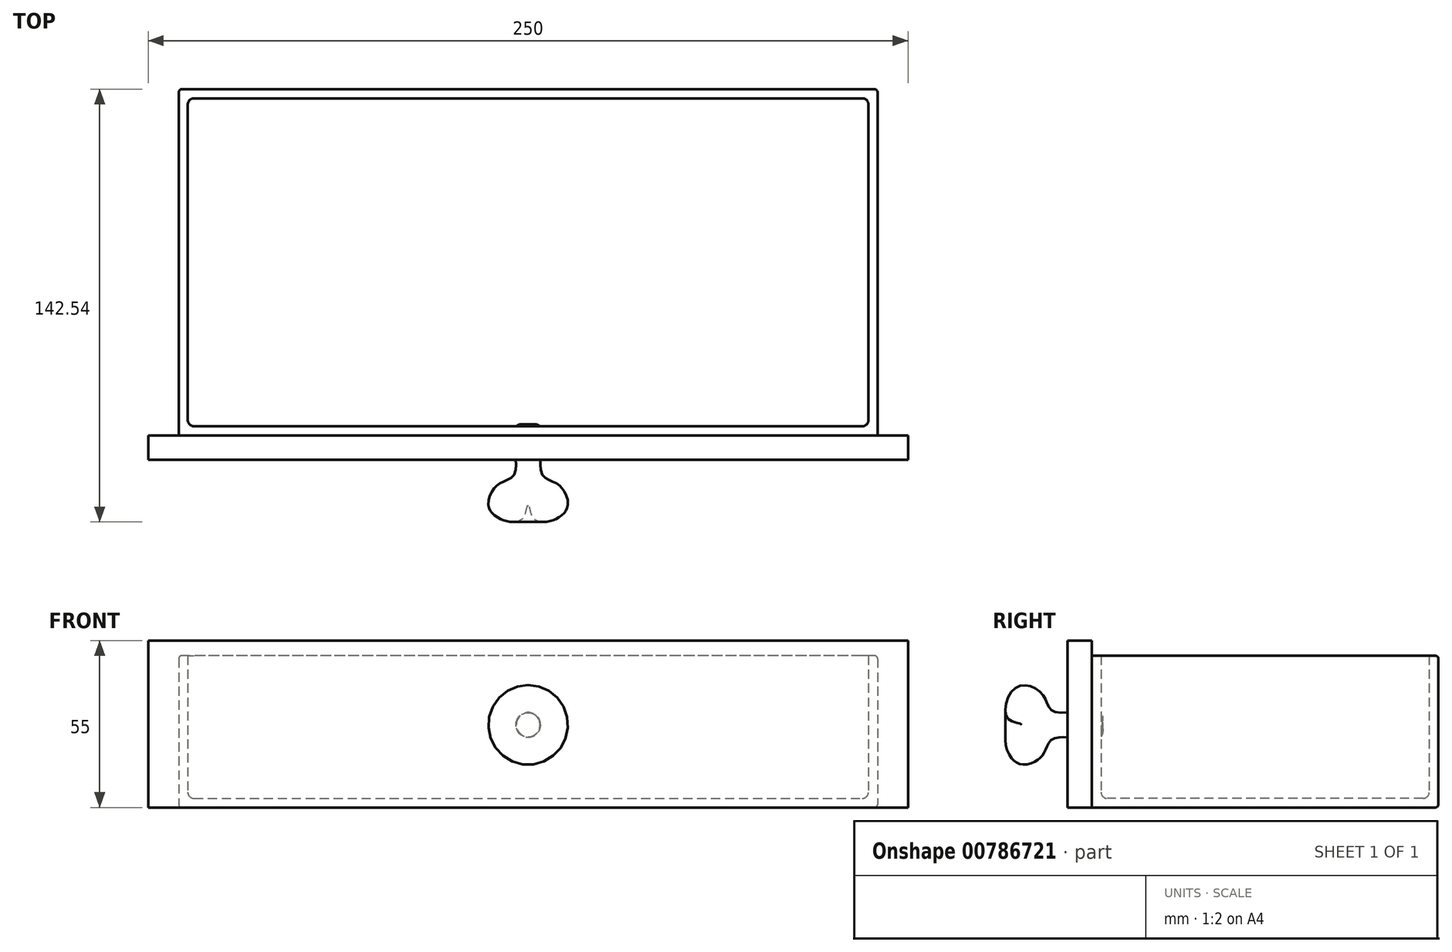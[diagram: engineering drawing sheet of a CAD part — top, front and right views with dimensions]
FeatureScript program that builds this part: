
annotation { "Feature Type Name" : "Feature", "Feature Type Description" : "" }
export const myFeature = defineFeature(function(context is Context, id is Id, definition is map)
    precondition{}
    {
        {
            var Q0;
            Q0=qCreatedBy(makeId("Top.planeOp"),FACE);
            var sketch = newSketch(context, id + "F0", { "sketchPlane" : qUnion([Q0])});
            skLineSegment(sketch, "E0.bottom", {"start": v(115, 60) * mm, "end": v(-115, 60) * mm});
            skLineSegment(sketch, "E0.right", {"start": v(-125, -54) * mm, "end": v(-125, -60) * mm});
            skPoint(sketch, "E0.middle", {"position": v(0, 0) * mm});
            skLineSegment(sketch, "E1", {"start": v(-115, 60) * mm, "end": v(-115, -54) * mm});
            skLineSegment(sketch, "E2", {"start": v(115, 60) * mm, "end": v(115, -54) * mm});
            skLineSegment(sketch, "E3", {"start": v(-115, -54) * mm, "end": v(115, -54) * mm});
            skPoint(sketch, "E4.orphan", {"position": v(125, 60) * mm});
            skPoint(sketch, "E5.orphan", {"position": v(-125, 60) * mm});
            skPoint(sketch, "E0.left.end.orphan", {"position": v(125, -60) * mm});
            skSolve(sketch);
        }
        {
            var Q0;
            Q0=qCreatedBy(makeId("Top.planeOp"),FACE);
            var sketch = newSketch(context, id + "F1", { "sketchPlane" : qUnion([Q0])});
            skLineSegment(sketch, "E6.bottom", {"start": v(125, -54) * mm, "end": v(-125, -54) * mm});
            skLineSegment(sketch, "E6.top", {"start": v(125, -62) * mm, "end": v(-125, -62) * mm});
            skLineSegment(sketch, "E6.left", {"start": v(125, -54) * mm, "end": v(125, -62) * mm});
            skLineSegment(sketch, "E6.right", {"start": v(-125, -54) * mm, "end": v(-125, -62) * mm});
            skPoint(sketch, "E6.middle", {"position": v(0, -58) * mm});
            skSolve(sketch);
        }
        {
            var Q0;
            Q0 = qSketchRegion(id + "F0", true);
            extrude(context, id + "F2", {"entities" : qUnion([Q0]), "depth" : 50 * mm, "offsetDistance" : 25 * mm});
        }
        {
            var Q0;
            Q0=makeQuery(id+"F2.opExtrude","CAP_FACE",FACE,{"disambiguationData":[OSD([sQuery(id+"F0.wireOp",EDGE,"E0.bottom"),sQuery(id+"F0.wireOp",EDGE,"E1"),sQuery(id+"F0.wireOp",EDGE,"E2"),sQuery(id+"F0.wireOp",EDGE,"E3")])],"isStart":false});
            shell(context, id + "F3", {"entities" : qUnion([Q0]), "thickness" : 3 * mm});
        }
        {
            var Q0;
            Q0=makeQuery(id+"F1.imprint","IMPRINT",FACE,{"disambiguationData":[TD([[makeQuery(id+"F1.imprint","IMPRINT",EDGE,{"derivedFrom":sQuery(id+"F1.wireOp",EDGE,"E6.bottom")}),1.0]])]});
            extrude(context, id + "F4", {"entities" : qUnion([Q0]), "operationType" : NewBodyOperationType.ADD, "depth" : 55 * mm, "offsetDistance" : 25 * mm});
        }
        {
            var Q0;
            Q0=makeQuery(id+"F3.opShell","OFFSET_FACE",FACE,{"disambiguationData":[OSD([sQuery(id+"F0.wireOp",EDGE,"E0.bottom"),sQuery(id+"F0.wireOp",EDGE,"E1"),sQuery(id+"F0.wireOp",EDGE,"E2"),sQuery(id+"F0.wireOp",EDGE,"E3")])]});
            fillet(context, id + "F5", {"entities" : qUnion([Q0]), "radius" : 2 * mm, "tangentPropagation" : true, "allowEdgeOverflow" : false});
        }
        {
            var Q0;
            Q0=makeQuery(id+"F3.opShell","OFFSET_EDGE",EDGE,{"disambiguationData":[OSD([sQuery(id+"F0.wireOp",EDGE,"E0.bottom"),sQuery(id+"F0.wireOp",EDGE,"E1")])]});
            var Q1;
            Q1=makeQuery(id+"F3.opShell","OFFSET_EDGE",EDGE,{"disambiguationData":[OSD([sQuery(id+"F0.wireOp",EDGE,"E1"),sQuery(id+"F0.wireOp",EDGE,"E3")])]});
            var Q2;
            Q2=makeQuery(id+"F3.opShell","OFFSET_EDGE",EDGE,{"disambiguationData":[OSD([sQuery(id+"F0.wireOp",EDGE,"E0.bottom"),sQuery(id+"F0.wireOp",EDGE,"E2")])]});
            var Q3;
            Q3=makeQuery(id+"F3.opShell","OFFSET_EDGE",EDGE,{"disambiguationData":[OSD([sQuery(id+"F0.wireOp",EDGE,"E2"),sQuery(id+"F0.wireOp",EDGE,"E3")])]});
            var Q4;
            Q4=makeQuery(id+"F3.opShell","OFFSET_FACE",FACE,{"disambiguationData":[OSD([sQuery(id+"F0.wireOp",EDGE,"E0.bottom"),sQuery(id+"F0.wireOp",EDGE,"E1"),sQuery(id+"F0.wireOp",EDGE,"E2"),sQuery(id+"F0.wireOp",EDGE,"E3")])]});
            var Q5;
            Q5=makeQuery(id+"F2.opExtrude","CAP_EDGE",EDGE,{"disambiguationData":[OSD([sQuery(id+"F0.wireOp",EDGE,"E3")])],"isStart":false});
            fillet(context, id + "F6", {"entities" : qUnion([Q0, Q1, Q2, Q3, Q4, Q5]), "radius" : 2 * mm, "tangentPropagation" : true, "allowEdgeOverflow" : false});
        }
        {
            var Q0;
            Q0=qCreatedBy(makeId("Right.planeOp"),FACE);
            var sketch = newSketch(context, id + "F7", { "sketchPlane" : qUnion([Q0])});
            skLineSegment(sketch, "E7", {"start": v(0, 27.2) * mm, "end": v(-118.17, 27.2) * mm});
            skFitSpline(sketch, "E8", {"points": [v(-50.7, 27.2) * mm, v(-51.42, 31.4) * mm, v(-66.47, 31.62) * mm, v(-70.17, 37.06) * mm, v(-78.86, 39.59) * mm, v(-81.6, 29.23) * mm, v(-77.16, 27.2) * mm], "startDerivative": vector(10, 39.32) * mm, "endDerivative": vector(-4.74, -17.25) * mm});
            skSolve(sketch);
        }
        {
            var Q0;
            {var subQ0=sQuery(id+"F7.wireOp",EDGE,"E8");Q0=makeQuery(id+"F7.imprint","IMPRINT",FACE,{"disambiguationData":[TD([[makeQuery(id+"F7.imprint","IMPRINT",EDGE,{"derivedFrom":subQ0}),1.0]])]});}
            var Q1;
            Q1=sQuery(id+"F7.wireOp",EDGE,"E7");
            revolve(context, id + "F8", {"operationType" : NewBodyOperationType.ADD, "surfaceOperationType" : NewSurfaceOperationType.NEW, "entities" : qUnion([Q0]), "axis" : qUnion([Q1]), "revolveType" : RevolveType.FULL});
        }
        {
            var Q0;
            Q0=makeQuery(id+"F2.opExtrude","CAP_EDGE",EDGE,{"disambiguationData":[OSD([sQuery(id+"F0.wireOp",EDGE,"E1")])],"isStart":true});
            var Q1;
            Q1=makeQuery(id+"F2.opExtrude","CAP_EDGE",EDGE,{"disambiguationData":[OSD([sQuery(id+"F0.wireOp",EDGE,"E0.bottom")])],"isStart":true});
            var Q2;
            Q2=makeQuery(id+"F2.opExtrude","CAP_EDGE",EDGE,{"disambiguationData":[OSD([sQuery(id+"F0.wireOp",EDGE,"E2")])],"isStart":true});
            var Q3;
            Q3=makeQuery(id+"F2.opExtrude","SWEPT_EDGE",EDGE,{"disambiguationData":[OSD([sQuery(id+"F0.wireOp",EDGE,"E2"),sQuery(id+"F0.wireOp",EDGE,"E3")])]});
            var Q4;
            Q4=makeQuery(id+"F2.opExtrude","SWEPT_EDGE",EDGE,{"disambiguationData":[OSD([sQuery(id+"F0.wireOp",EDGE,"E0.bottom"),sQuery(id+"F0.wireOp",EDGE,"E2")])]});
            var Q5;
            Q5=makeQuery(id+"F2.opExtrude","CAP_EDGE",EDGE,{"disambiguationData":[OSD([sQuery(id+"F0.wireOp",EDGE,"E2")])],"isStart":false});
            var Q6;
            Q6=makeQuery(id+"F2.opExtrude","CAP_EDGE",EDGE,{"disambiguationData":[OSD([sQuery(id+"F0.wireOp",EDGE,"E0.bottom")])],"isStart":false});
            var Q7;
            Q7=makeQuery(id+"F2.opExtrude","SWEPT_EDGE",EDGE,{"disambiguationData":[OSD([sQuery(id+"F0.wireOp",EDGE,"E0.bottom"),sQuery(id+"F0.wireOp",EDGE,"E1")])]});
            var Q8;
            Q8=makeQuery(id+"F2.opExtrude","CAP_EDGE",EDGE,{"disambiguationData":[OSD([sQuery(id+"F0.wireOp",EDGE,"E1")])],"isStart":false});
            var Q9;
            Q9=makeQuery(id+"F2.opExtrude","SWEPT_EDGE",EDGE,{"disambiguationData":[OSD([sQuery(id+"F0.wireOp",EDGE,"E1"),sQuery(id+"F0.wireOp",EDGE,"E3")])]});
            fillet(context, id + "F9", {"entities" : qUnion([Q0, Q1, Q2, Q3, Q4, Q5, Q6, Q7, Q8, Q9]), "radius" : 1 * mm, "tangentPropagation" : true, "allowEdgeOverflow" : false});
        }
    });
